# Revit family: Toilet_Seat-Elongated_Closed_Front-KOHLER-Purefresh-K-5588
name_source: partatom
category: Specialty Equipment
revit_build: Autodesk Revit 2015 (Build: 20140606_1530(x64)
units: mm (PartAtom-declared; Revit-internal decimal feet)

## types (2) — shared parameters
ADA Compliant = No
Assembly Code = C1030200
Date Modified = 11/19/2018
Default Elevation = 42"
Description = Elongated toilet seat
Electrical Note = Battery-operated - no electrical cords required, Up to 6 months of battery life (uses 2 D batteries, not included)
Height = 2 1/2"
Length = 19 3/16"
Manufacturer = KOHLER Co.
MasterFormat 1995 = 10820
MasterFormat 2004 = 10.28.13
Material = Polypropylene Plastic
Product Documentation Link = http://www.us.kohler.com
Product Name = Purefresh
Product Page URL = http://www.us.kohler.com
URL = https://www.us.kohler.com
Width = 14 3/16"

## per-type parameters (varying)
| type | Finish | Model | Type |
| 0-White | Kohler-Plastic-0-White | K-5588-0 | 1 |
| 96-Biscuit | Kohler-Plastic-96-Biscuit | K-5588-96 | 2 |

## geometry (parser evidence)
native form markers: Sweep x8
no freeform markers — native parametric forms only
